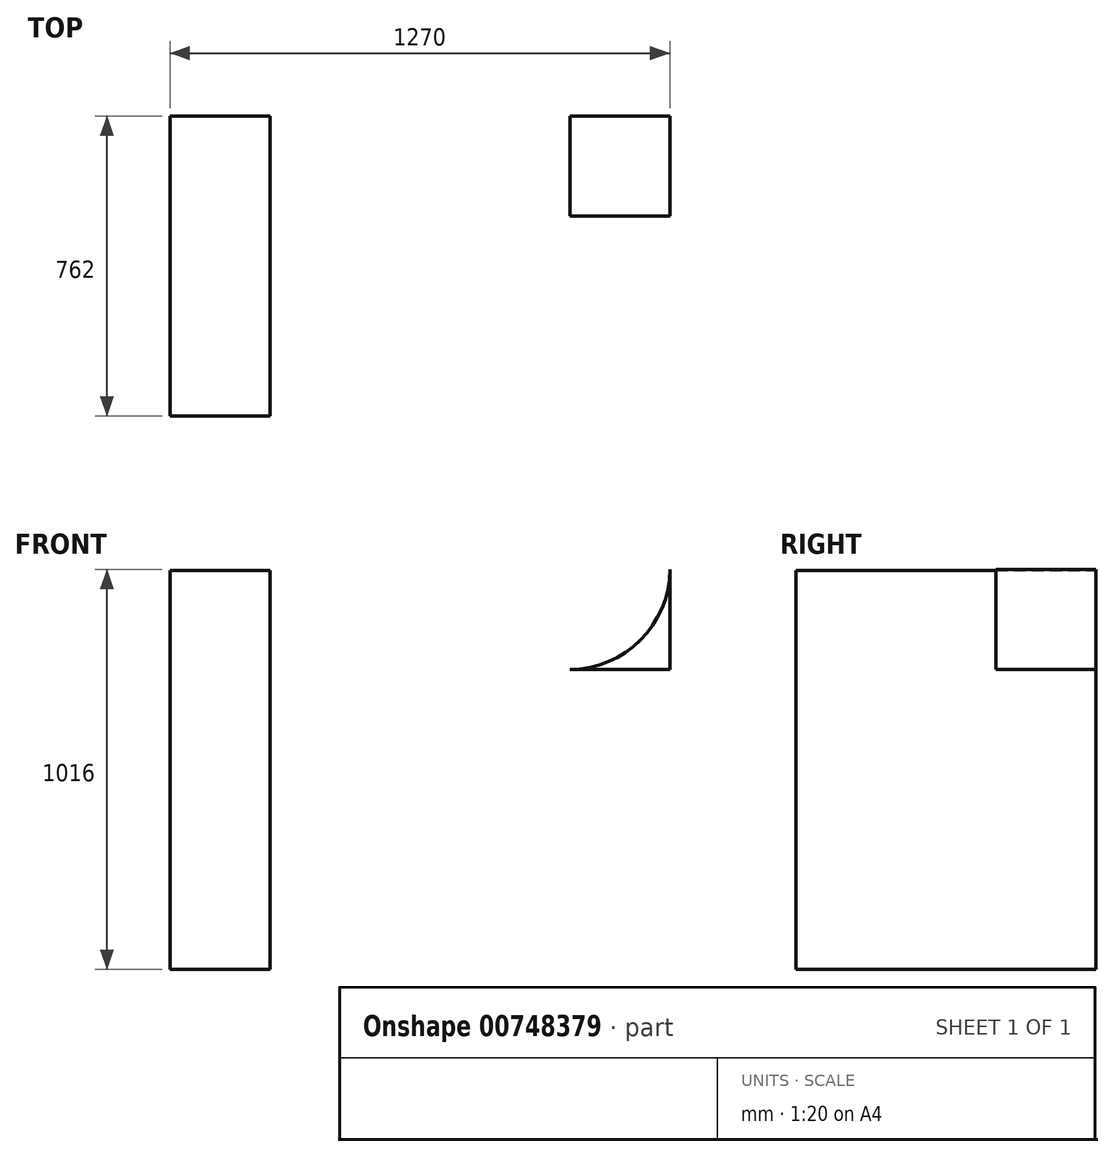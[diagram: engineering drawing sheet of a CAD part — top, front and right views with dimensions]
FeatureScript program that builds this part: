
annotation { "Feature Type Name" : "Feature", "Feature Type Description" : "" }
export const myFeature = defineFeature(function(context is Context, id is Id, definition is map)
    precondition{}
    {
        {
            var Q0;
            Q0=qCreatedBy(makeId("Front.planeOp"),FACE);
            var sketch = newSketch(context, id + "F0", { "sketchPlane" : qUnion([Q0])});
            skLineSegment(sketch, "E0", {"start": v(0, 254) * mm, "end": v(0, -762) * mm});
            skLineSegment(sketch, "E1", {"start": v(0, -762) * mm, "end": v(501.65, -762) * mm});
            skLineSegment(sketch, "E2", {"start": v(508, -755.65) * mm, "end": v(508, 0) * mm});
            skLineSegment(sketch, "E3", {"start": v(508, 0) * mm, "end": v(1270, 0) * mm});
            skLineSegment(sketch, "E4", {"start": v(1270, 0) * mm, "end": v(1270, 254) * mm});
            skLineSegment(sketch, "E5", {"start": v(1270, 254) * mm, "end": v(0, 254) * mm});
            skPoint(sketch, "E6.visualSharp", {"position": v(508, -762) * mm});
            skArc(sketch, "E6.filletArc", {"start": v(501.65, -762) * mm, "mid": v(506.14, -760.14) * mm, "end": v(508, -755.65) * mm});
            skSolve(sketch);
        }
        {
            var Q0;
            Q0=makeQuery(id+"F0.imprint","IMPRINT",FACE,{"disambiguationData":[TD([[makeQuery(id+"F0.imprint","IMPRINT",EDGE,{"derivedFrom":sQuery(id+"F0.wireOp",EDGE,"E0")}),1.0]])]});
            var sketch = newSketch(context, id + "F1", { "sketchPlane" : qUnion([Q0])});
            skLineSegment(sketch, "E7", {"start": v(0, -764.37) * mm, "end": v(0, 251.63) * mm});
            skLineSegment(sketch, "E8", {"start": v(0, 251.63) * mm, "end": v(254, 251.63) * mm});
            skLineSegment(sketch, "E9", {"start": v(254, 251.63) * mm, "end": v(254, -764.37) * mm});
            skLineSegment(sketch, "E10", {"start": v(254, -764.37) * mm, "end": v(0, -764.37) * mm});
            skSolve(sketch);
        }
        {
            var Q0;
            {var subQ3=sQuery(id+"F1.wireOp",EDGE,"E8");Q0=makeQuery(id+"F1.imprint","IMPRINT",FACE,{"disambiguationData":[TD([[makeQuery(id+"F1.imprint","IMPRINT",EDGE,{"derivedFrom":subQ3}),-1.0]])]});}
            extrude(context, id + "F2", {"entities" : qUnion([Q0]), "depth" : 762 * mm, "offsetDistance" : 25.4 * mm});
        }
        {
            var Q0;
            Q0 = qSketchRegion(id + "F0", true);
            extrude(context, id + "F3", {"entities" : qUnion([Q0]), "operationType" : NewBodyOperationType.ADD, "depth" : 254 * mm, "offsetDistance" : 25.4 * mm});
        }
        {
            var Q0;
            Q0=makeQuery(id+"F3.opExtrude","CAP_FACE",FACE,{"disambiguationData":[OSD([sQuery(id+"F0.wireOp",EDGE,"E0"),sQuery(id+"F0.wireOp",EDGE,"E1"),sQuery(id+"F0.wireOp",EDGE,"E2"),sQuery(id+"F0.wireOp",EDGE,"E3"),sQuery(id+"F0.wireOp",EDGE,"E4"),sQuery(id+"F0.wireOp",EDGE,"E5"),sQuery(id+"F0.wireOp",EDGE,"E6.filletArc")])],"isStart":false});
            var sketch = newSketch(context, id + "F4", { "sketchPlane" : qUnion([Q0])});
            skArc(sketch, "E11", {"start": v(254, -762) * mm, "mid": v(433.6, -687.6) * mm, "end": v(508, -508) * mm});
            skSolve(sketch);
        }
        {
            var Q0;
            {var subQ0=sQuery(id+"F4.wireOp",EDGE,"E11");Q0=makeQuery(id+"F4.imprint","IMPRINT",FACE,{"disambiguationData":[TD([[makeQuery(id+"F4.imprint","IMPRINT",EDGE,{"derivedFrom":subQ0}),-1.0]])]});}
            extrude(context, id + "F5", {"entities" : qUnion([Q0]), "operationType" : NewBodyOperationType.REMOVE, "oppositeDirection" : true, "depth" : 327.66 * mm, "offsetDistance" : 25.4 * mm});
        }
        {
            var Q0;
            Q0=makeQuery(id+"F3.opExtrude","CAP_FACE",FACE,{"disambiguationData":[OSD([sQuery(id+"F0.wireOp",EDGE,"E0"),sQuery(id+"F0.wireOp",EDGE,"E1"),sQuery(id+"F0.wireOp",EDGE,"E2"),sQuery(id+"F0.wireOp",EDGE,"E3"),sQuery(id+"F0.wireOp",EDGE,"E4"),sQuery(id+"F0.wireOp",EDGE,"E5"),sQuery(id+"F0.wireOp",EDGE,"E6.filletArc")])],"isStart":false});
            var sketch = newSketch(context, id + "F6", { "sketchPlane" : qUnion([Q0])});
            skArc(sketch, "E12", {"start": v(1270, 254) * mm, "mid": v(1195.6, 74.4) * mm, "end": v(1016, 0) * mm});
            skSolve(sketch);
        }
        {
            var Q0;
            {var subQ0=sQuery(id+"F6.wireOp",EDGE,"E12");Q0=makeQuery(id+"F6.imprint","IMPRINT",FACE,{"disambiguationData":[TD([[makeQuery(id+"F6.imprint","IMPRINT",EDGE,{"derivedFrom":subQ0}),1.0]])]});}
            extrude(context, id + "F7", {"entities" : qUnion([Q0]), "operationType" : NewBodyOperationType.REMOVE, "oppositeDirection" : true, "depth" : 401.32 * mm, "offsetDistance" : 25.4 * mm});
        }
    });
